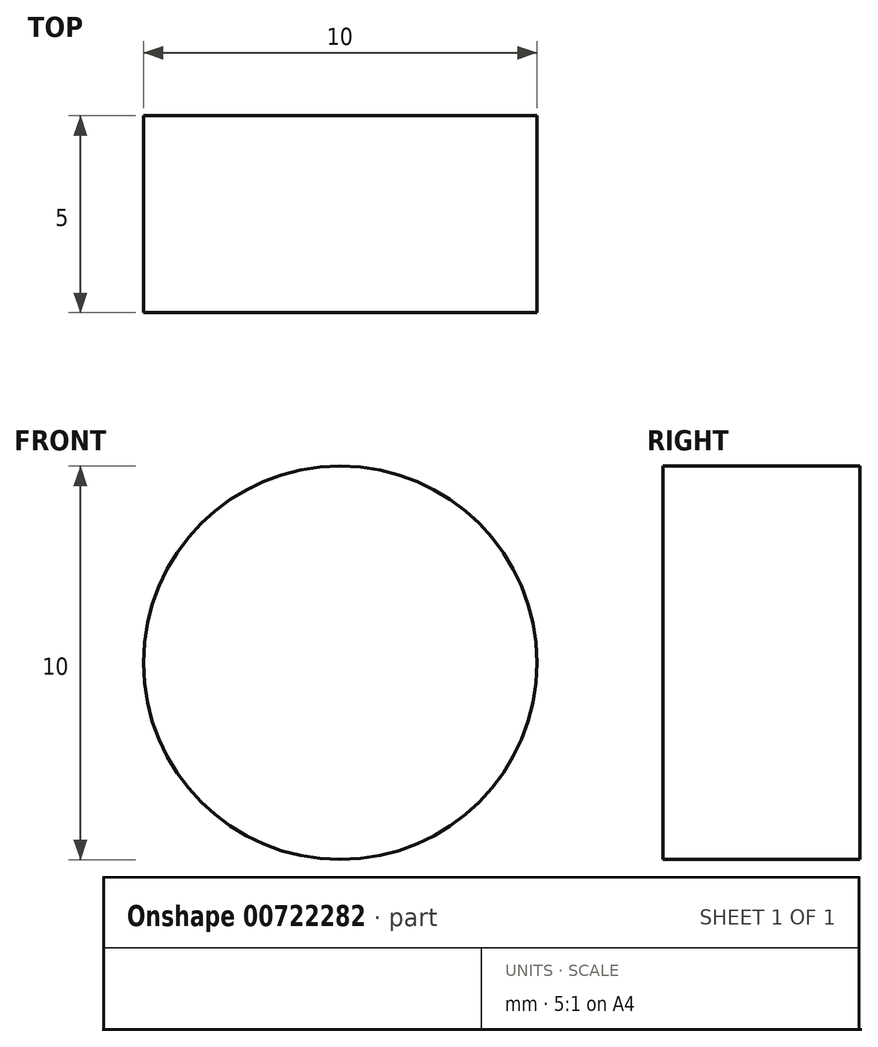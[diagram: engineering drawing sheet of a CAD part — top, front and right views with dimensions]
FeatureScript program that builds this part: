
annotation { "Feature Type Name" : "Feature", "Feature Type Description" : "" }
export const myFeature = defineFeature(function(context is Context, id is Id, definition is map)
    precondition{}
    {
        {
            var Q0;
            Q0=qCreatedBy(makeId("Front.planeOp"),FACE);
            var sketch = newSketch(context, id + "F0", { "sketchPlane" : qUnion([Q0])});
            skCircle(sketch, "E0", {"center": v(0, 13.72) * mm, "radius": 5 * mm});
            skSolve(sketch);
        }
        {
            var Q0;
            Q0=makeQuery(id+"F0.imprint","IMPRINT",FACE,{"disambiguationData":[TD([[makeQuery(id+"F0.imprint","IMPRINT",EDGE,{"derivedFrom":sQuery(id+"F0.wireOp",EDGE,"E0")}),1.0]])]});
            extrude(context, id + "F1", {"entities" : qUnion([Q0]), "depth" : 5 * mm, "offsetDistance" : 25 * mm});
        }
    });
